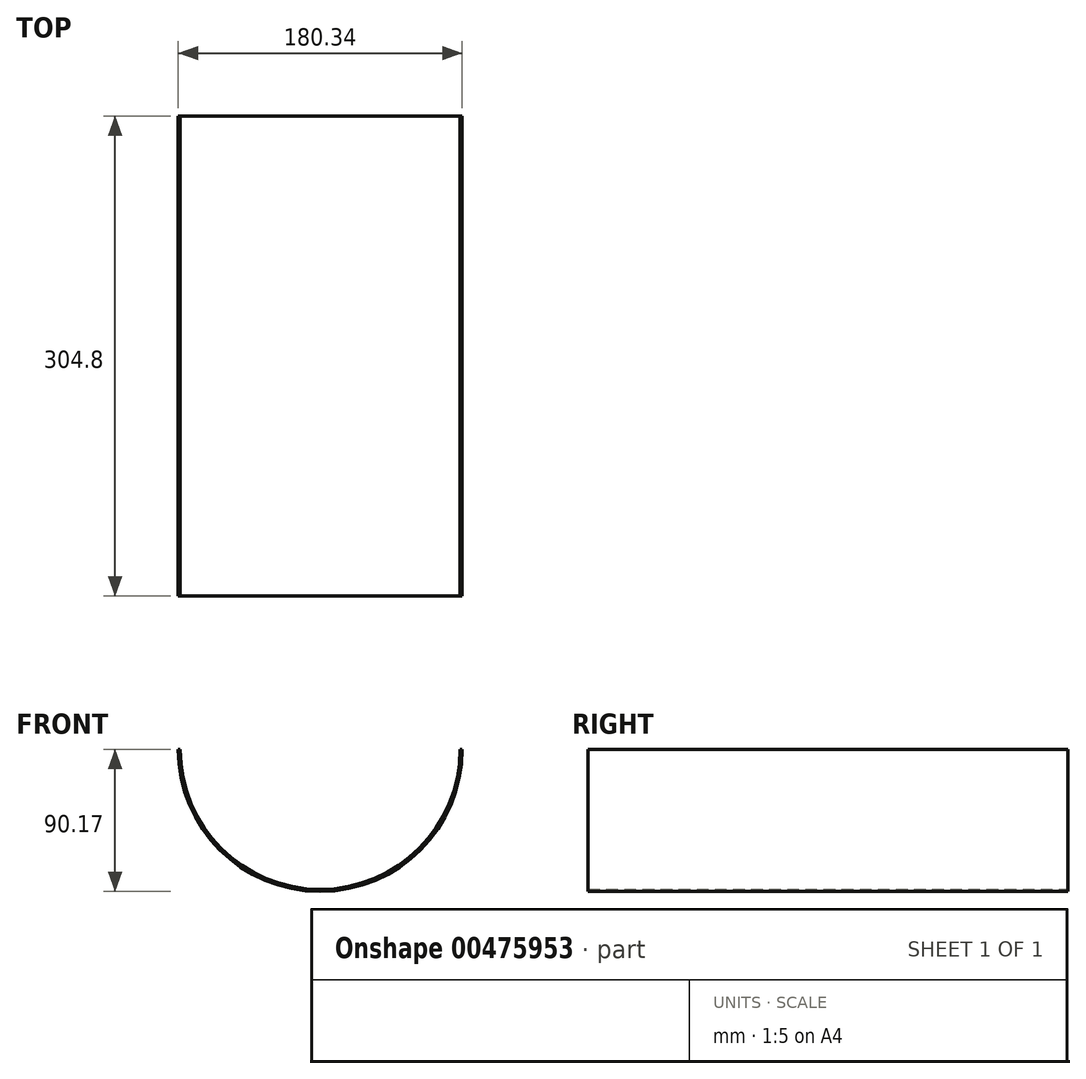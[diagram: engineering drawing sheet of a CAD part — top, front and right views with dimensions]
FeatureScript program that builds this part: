
annotation { "Feature Type Name" : "Feature", "Feature Type Description" : "" }
export const myFeature = defineFeature(function(context is Context, id is Id, definition is map)
    precondition{}
    {
        {
            var Q0;
            Q0=qCreatedBy(makeId("Front.planeOp"),FACE);
            var sketch = newSketch(context, id + "F0", { "sketchPlane" : qUnion([Q0])});
            skArc(sketch, "E0", {"start": v(-90.17, 0) * mm, "mid": v(0, -90.17) * mm, "end": v(90.17, 0) * mm});
            skArc(sketch, "E1", {"start": v(-88.9, 0) * mm, "mid": v(0, -88.9) * mm, "end": v(88.9, 0) * mm});
            skLineSegment(sketch, "E2", {"start": v(-90.17, 0) * mm, "end": v(-88.9, 0) * mm});
            skLineSegment(sketch, "E3", {"start": v(90.17, 0) * mm, "end": v(88.9, 0) * mm});
            skSolve(sketch);
        }
        {
            var Q0;
            Q0=qSketchRegion(id+"F0",true);
            extrude(context, id + "F1", {"entities" : qUnion([Q0]), "depth" : 152.4 * mm});
        }
        {
            var Q0;
            Q0=makeQuery(id+"F1.opExtrude","CAP_FACE",FACE,{"disambiguationData":[OSD([sQuery(id+"F0.wireOp",EDGE,"E0"),sQuery(id+"F0.wireOp",EDGE,"E1"),sQuery(id+"F0.wireOp",EDGE,"E2"),sQuery(id+"F0.wireOp",EDGE,"E3")])],"isStart":true});
            extrude(context, id + "F2", {"entities" : qUnion([Q0]), "operationType" : NewBodyOperationType.ADD, "depth" : 152.4 * mm});
        }
    });
